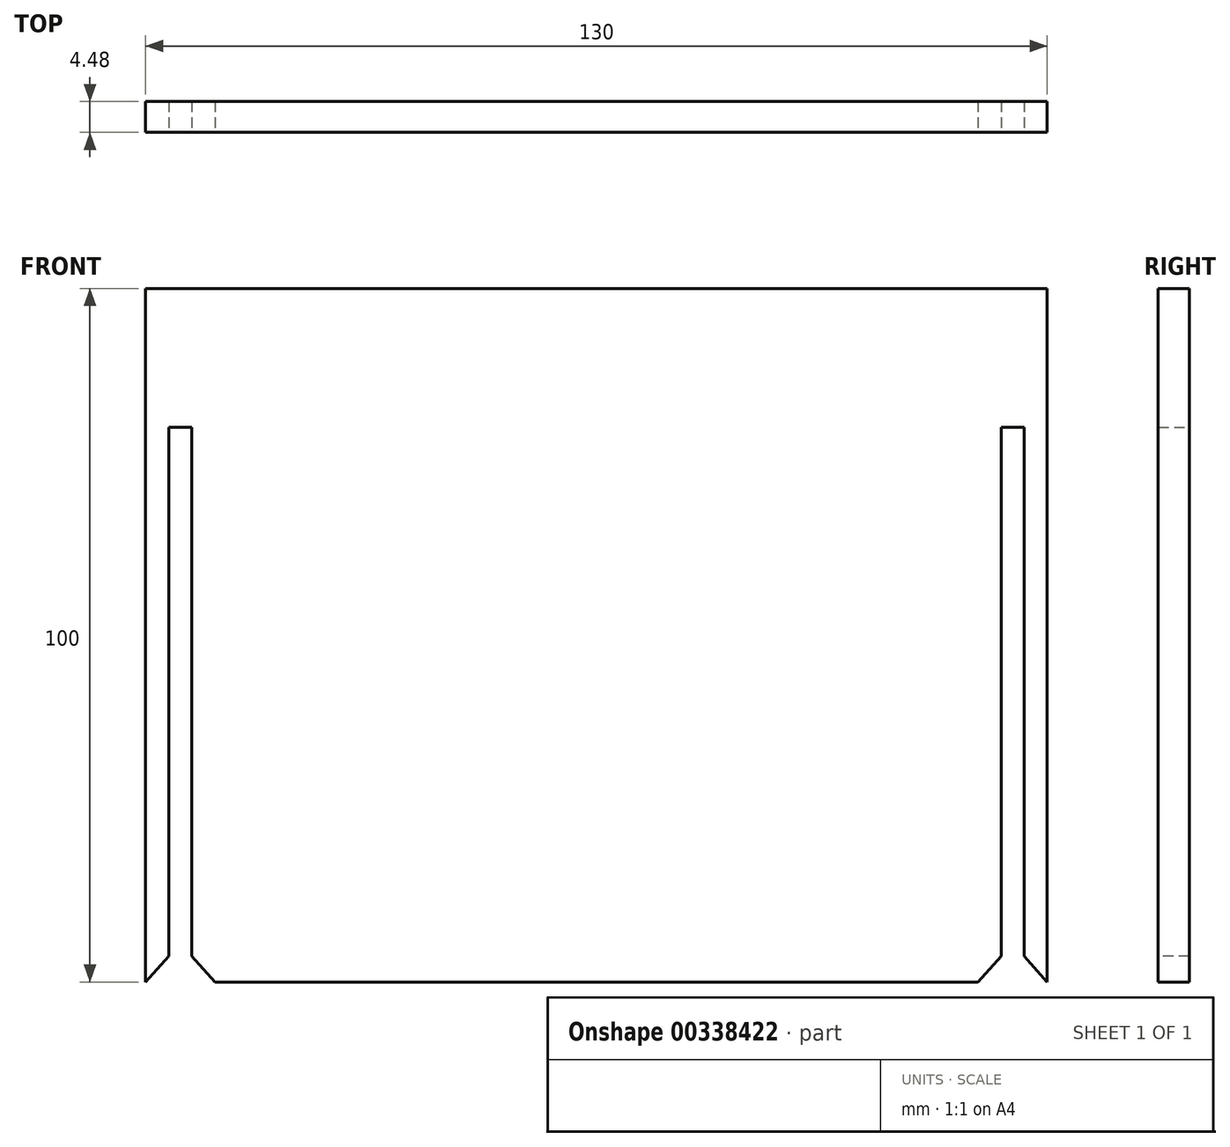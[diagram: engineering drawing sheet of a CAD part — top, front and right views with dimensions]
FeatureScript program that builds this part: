
annotation { "Feature Type Name" : "Feature", "Feature Type Description" : "" }
export const myFeature = defineFeature(function(context is Context, id is Id, definition is map)
    precondition{}
    {
        {
            var Q0;
            Q0=qCreatedBy(makeId("Top.planeOp"),FACE);
            var sketch = newSketch(context, id + "F0", { "sketchPlane" : qUnion([Q0])});
            skLineSegment(sketch, "E0.top", {"start": v(-26.06, 2.24) * mm, "end": v(103.94, 2.24) * mm});
            skLineSegment(sketch, "E0.left", {"start": v(-26.06, 0) * mm, "end": v(-26.06, 2.24) * mm});
            skLineSegment(sketch, "E0.right", {"start": v(103.94, 0) * mm, "end": v(103.94, 2.24) * mm});
            skLineSegment(sketch, "E1.MirrorCS", {"start": v(-26.06, 0) * mm, "end": v(-26.06, -2.24) * mm});
            skLineSegment(sketch, "E2.MirrorCS", {"start": v(-26.06, -2.24) * mm, "end": v(103.94, -2.24) * mm});
            skLineSegment(sketch, "E3.MirrorCS", {"start": v(103.94, 0) * mm, "end": v(103.94, -2.24) * mm});
            skSolve(sketch);
        }
        {
            var Q0;
            Q0=makeQuery(id+"F0.imprint","IMPRINT",FACE,{"disambiguationData":[TD([[makeQuery(id+"F0.imprint","IMPRINT",EDGE,{"derivedFrom":sQuery(id+"F0.wireOp",EDGE,"E0.top")}),-1.0]])]});
            extrude(context, id + "F1", {"entities" : qUnion([Q0]), "depth" : 100 * mm});
        }
        {
            var Q0;
            Q0=makeQuery(id+"F1.opExtrude","CAP_FACE",FACE,{"disambiguationData":[OSD([sQuery(id+"F0.wireOp",EDGE,"E0.top"),sQuery(id+"F0.wireOp",EDGE,"E0.left"),sQuery(id+"F0.wireOp",EDGE,"E0.right"),sQuery(id+"F0.wireOp",EDGE,"E1.MirrorCS"),sQuery(id+"F0.wireOp",EDGE,"E2.MirrorCS"),sQuery(id+"F0.wireOp",EDGE,"E3.MirrorCS")])],"isStart":true});
            var sketch = newSketch(context, id + "F2", { "sketchPlane" : qUnion([Q0])});
            skLineSegment(sketch, "E4.bottom", {"start": v(-22.7, 2.24) * mm, "end": v(-19.41, 2.24) * mm});
            skLineSegment(sketch, "E4.top", {"start": v(-22.7, -2.24) * mm, "end": v(-19.41, -2.24) * mm});
            skLineSegment(sketch, "E4.left", {"start": v(-22.7, 2.24) * mm, "end": v(-22.7, -2.24) * mm});
            skLineSegment(sketch, "E4.right", {"start": v(-19.41, 2.24) * mm, "end": v(-19.41, -2.24) * mm});
            skLineSegment(sketch, "E5.bottom", {"start": v(-19.41, 2.24) * mm, "end": v(-16.06, 2.24) * mm});
            skLineSegment(sketch, "E5.top", {"start": v(-19.41, -2.24) * mm, "end": v(-16.06, -2.24) * mm});
            skLineSegment(sketch, "E5.right", {"start": v(-16.06, 2.24) * mm, "end": v(-16.06, -2.24) * mm});
            skSolve(sketch);
        }
        {
            var Q0;
            Q0=makeQuery(id+"F2.imprint","IMPRINT",FACE,{"disambiguationData":[TD([[makeQuery(id+"F2.imprint","IMPRINT",EDGE,{"derivedFrom":sQuery(id+"F2.wireOp",EDGE,"E4.bottom")}),-1.0]])]});
            extrude(context, id + "F3", {"entities" : qUnion([Q0]), "operationType" : NewBodyOperationType.REMOVE, "oppositeDirection" : true, "depth" : 80 * mm});
        }
        {
            var Q0;
            {var subQ0=sQuery(id+"F0.wireOp",EDGE,"E0.top");var subQ1=sQuery(id+"F0.wireOp",EDGE,"E2.MirrorCS");var subQ2=sQuery(id+"F0.wireOp",EDGE,"E3.MirrorCS");var subQ3=sQuery(id+"F0.wireOp",EDGE,"E0.right");Q0=makeQuery(id+"F3.boolean.opBoolean","SPLIT",FACE,{"disambiguationData":[TD([makeQuery(id+"F3.opExtrude","SWEPT_FACE",FACE,{"disambiguationData":[OSD([sQuery(id+"F2.wireOp",EDGE,"E4.right")])]})])],"derivedFrom":makeQuery(id+"F1.opExtrude","CAP_FACE",FACE,{"disambiguationData":[OSD([subQ0,sQuery(id+"F0.wireOp",EDGE,"E0.left"),subQ3,sQuery(id+"F0.wireOp",EDGE,"E1.MirrorCS"),subQ1,subQ2])],"isStart":true})});}
            var sketch = newSketch(context, id + "F4", { "sketchPlane" : qUnion([Q0])});
            skLineSegment(sketch, "E6.bottom", {"start": v(100.59, 2.24) * mm, "end": v(97.3, 2.24) * mm});
            skLineSegment(sketch, "E6.top", {"start": v(100.59, -2.24) * mm, "end": v(97.3, -2.24) * mm});
            skLineSegment(sketch, "E6.left", {"start": v(100.59, 2.24) * mm, "end": v(100.59, -2.24) * mm});
            skLineSegment(sketch, "E6.right", {"start": v(97.3, 2.24) * mm, "end": v(97.3, -2.24) * mm});
            skSolve(sketch);
        }
        {
            var Q0;
            Q0=makeQuery(id+"F4.imprint","IMPRINT",FACE,{"disambiguationData":[TD([[makeQuery(id+"F4.imprint","IMPRINT",EDGE,{"derivedFrom":sQuery(id+"F4.wireOp",EDGE,"E6.bottom")}),-1.0]])]});
            extrude(context, id + "F5", {"entities" : qUnion([Q0]), "operationType" : NewBodyOperationType.REMOVE, "oppositeDirection" : true, "depth" : 80 * mm});
        }
        {
            var Q0;
            Q0=makeQuery(id+"F1.opExtrude","SWEPT_FACE",FACE,{"disambiguationData":[OSD([sQuery(id+"F0.wireOp",EDGE,"E2.MirrorCS")])]});
            var sketch = newSketch(context, id + "F6", { "sketchPlane" : qUnion([Q0])});
            skLineSegment(sketch, "E7", {"start": v(-26.06, 0) * mm, "end": v(-22.7, 3.72) * mm});
            skLineSegment(sketch, "E8", {"start": v(-22.7, 3.72) * mm, "end": v(-19.41, 3.72) * mm});
            skLineSegment(sketch, "E9", {"start": v(-19.41, 3.72) * mm, "end": v(-16.06, 0) * mm});
            skSolve(sketch);
        }
        {
            var Q0;
            {var subQ0=sQuery(id+"F6.wireOp",EDGE,"E7");Q0=makeQuery(id+"F6.imprint","IMPRINT",FACE,{"disambiguationData":[TD([[makeQuery(id+"F6.imprint","IMPRINT",EDGE,{"derivedFrom":subQ0}),-1.0]])]});}
            var Q1;
            {var subQ0=sQuery(id+"F6.wireOp",EDGE,"E9");Q1=makeQuery(id+"F6.imprint","IMPRINT",FACE,{"disambiguationData":[TD([[makeQuery(id+"F6.imprint","IMPRINT",EDGE,{"derivedFrom":subQ0}),-1.0]])]});}
            extrude(context, id + "F7", {"entities" : qUnion([Q0, Q1]), "operationType" : NewBodyOperationType.REMOVE, "oppositeDirection" : true, "depth" : 25 * mm});
        }
        {
            var Q0;
            Q0=makeQuery(id+"F1.opExtrude","SWEPT_FACE",FACE,{"disambiguationData":[OSD([sQuery(id+"F0.wireOp",EDGE,"E2.MirrorCS")])]});
            var sketch = newSketch(context, id + "F8", { "sketchPlane" : qUnion([Q0])});
            skLineSegment(sketch, "E10", {"start": v(103.94, 0) * mm, "end": v(100.59, 3.72) * mm});
            skLineSegment(sketch, "E11", {"start": v(100.59, 3.72) * mm, "end": v(97.3, 3.72) * mm});
            skLineSegment(sketch, "E12", {"start": v(97.3, 3.72) * mm, "end": v(93.94, 0) * mm});
            skSolve(sketch);
        }
        {
            var Q0;
            {var subQ0=sQuery(id+"F8.wireOp",EDGE,"E12");Q0=makeQuery(id+"F8.imprint","IMPRINT",FACE,{"disambiguationData":[TD([[makeQuery(id+"F8.imprint","IMPRINT",EDGE,{"derivedFrom":subQ0}),1.0]])]});}
            var Q1;
            {var subQ0=sQuery(id+"F8.wireOp",EDGE,"E10");Q1=makeQuery(id+"F8.imprint","IMPRINT",FACE,{"disambiguationData":[TD([[makeQuery(id+"F8.imprint","IMPRINT",EDGE,{"derivedFrom":subQ0}),1.0]])]});}
            extrude(context, id + "F9", {"entities" : qUnion([Q0, Q1]), "operationType" : NewBodyOperationType.REMOVE, "oppositeDirection" : true, "depth" : 25 * mm});
        }
    });
